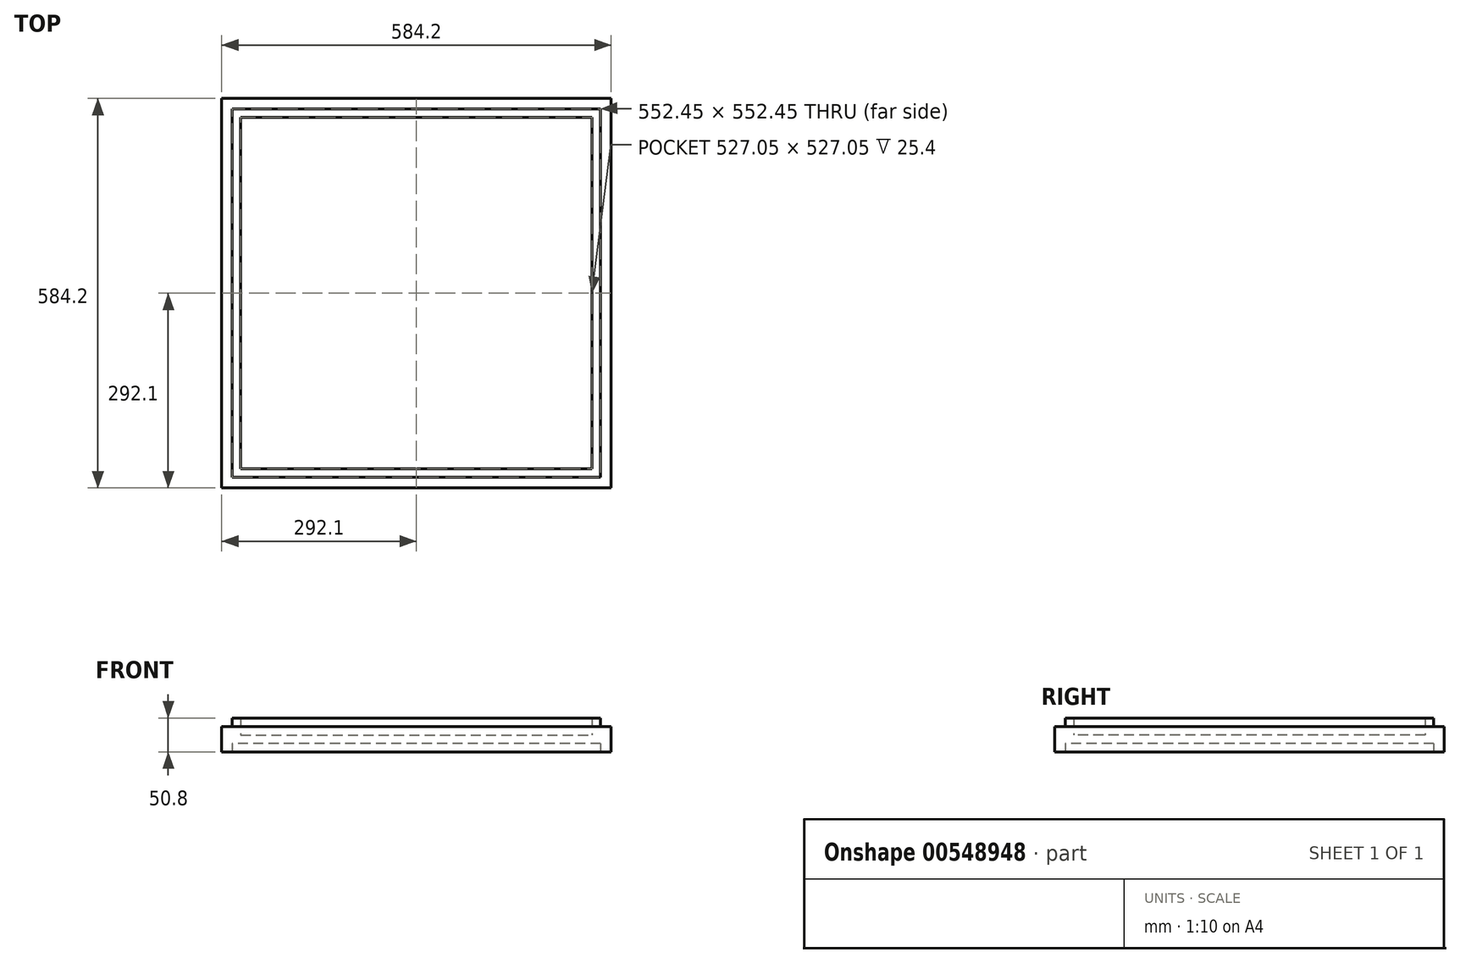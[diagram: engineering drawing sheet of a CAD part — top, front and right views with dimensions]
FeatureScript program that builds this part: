
annotation { "Feature Type Name" : "Feature", "Feature Type Description" : "" }
export const myFeature = defineFeature(function(context is Context, id is Id, definition is map)
    precondition{}
    {
        {
            var Q0;
            Q0=qCreatedBy(makeId("Top.planeOp"),FACE);
            var sketch = newSketch(context, id + "F0", { "sketchPlane" : qUnion([Q0])});
            skLineSegment(sketch, "E0.bottom", {"start": v(-292.1, 292.1) * mm, "end": v(292.1, 292.1) * mm});
            skLineSegment(sketch, "E0.top", {"start": v(-292.1, -292.1) * mm, "end": v(292.1, -292.1) * mm});
            skLineSegment(sketch, "E0.left", {"start": v(-292.1, 292.1) * mm, "end": v(-292.1, -292.1) * mm});
            skLineSegment(sketch, "E0.right", {"start": v(292.1, 292.1) * mm, "end": v(292.1, -292.1) * mm});
            skPoint(sketch, "E0.middle", {"position": v(0, 0) * mm});
            skSolve(sketch);
        }
        {
            var Q0;
            Q0=qSketchRegion(id+"F0",true);
            extrude(context, id + "F1", {"entities" : qUnion([Q0]), "depth" : 12.7 * mm, "offsetDistance" : 25.4 * mm});
        }
        {
            var Q0;
            Q0=makeQuery(id+"F1.opExtrude","CAP_FACE",FACE,{"disambiguationData":[OSD([sQuery(id+"F0.wireOp",EDGE,"E0.bottom"),sQuery(id+"F0.wireOp",EDGE,"E0.top"),sQuery(id+"F0.wireOp",EDGE,"E0.left"),sQuery(id+"F0.wireOp",EDGE,"E0.right")])],"isStart":false});
            var sketch = newSketch(context, id + "F2", { "sketchPlane" : qUnion([Q0])});
            skLineSegment(sketch, "E1.bottom", {"start": v(-292.1, 292.1) * mm, "end": v(292.1, 292.1) * mm});
            skLineSegment(sketch, "E1.top", {"start": v(-292.1, -292.1) * mm, "end": v(292.1, -292.1) * mm});
            skLineSegment(sketch, "E1.left", {"start": v(-292.1, 292.1) * mm, "end": v(-292.1, -292.1) * mm});
            skLineSegment(sketch, "E1.right", {"start": v(292.1, 292.1) * mm, "end": v(292.1, -292.1) * mm});
            skLineSegment(sketch, "E2.bottom", {"start": v(-279.4, 279.4) * mm, "end": v(279.4, 279.4) * mm});
            skLineSegment(sketch, "E2.top", {"start": v(-279.4, -279.4) * mm, "end": v(279.4, -279.4) * mm});
            skLineSegment(sketch, "E2.left", {"start": v(-279.4, 279.4) * mm, "end": v(-279.4, -279.4) * mm});
            skLineSegment(sketch, "E2.right", {"start": v(279.4, 279.4) * mm, "end": v(279.4, -279.4) * mm});
            skSolve(sketch);
        }
        {
            var Q0;
            Q0=qSketchRegion(id+"F2",true);
            extrude(context, id + "F3", {"entities" : qUnion([Q0]), "operationType" : NewBodyOperationType.ADD, "depth" : 152.4 * mm, "offsetDistance" : 25.4 * mm});
        }
        {
            var Q0;
            Q0=makeQuery(id+"F1.opExtrude","CAP_FACE",FACE,{"disambiguationData":[OSD([sQuery(id+"F0.wireOp",EDGE,"E0.bottom"),sQuery(id+"F0.wireOp",EDGE,"E0.top"),sQuery(id+"F0.wireOp",EDGE,"E0.left"),sQuery(id+"F0.wireOp",EDGE,"E0.right")])],"isStart":false});
            var sketch = newSketch(context, id + "F4", { "sketchPlane" : qUnion([Q0])});
            skLineSegment(sketch, "E3.bottom", {"start": v(-508.77, -441.53) * mm, "end": v(508.77, -441.53) * mm});
            skLineSegment(sketch, "E3.top", {"start": v(-508.77, 441.53) * mm, "end": v(508.77, 441.53) * mm});
            skLineSegment(sketch, "E3.left", {"start": v(-508.77, -441.53) * mm, "end": v(-508.77, 441.53) * mm});
            skLineSegment(sketch, "E3.right", {"start": v(508.77, -441.53) * mm, "end": v(508.77, 441.53) * mm});
            skPoint(sketch, "E3.middle", {"position": v(0, 0) * mm});
            skSolve(sketch);
        }
        {
            var Q0;
            Q0=makeQuery(id+"F4.imprint","IMPRINT",FACE,{"disambiguationData":[TD([[makeQuery(id+"F4.imprint","IMPRINT",EDGE,{"derivedFrom":sQuery(id+"F4.wireOp",EDGE,"E3.bottom")}),1.0]])]});
            extrude(context, id + "F5", {"entities" : qUnion([Q0]), "operationType" : NewBodyOperationType.REMOVE, "depth" : 508 * mm, "offsetDistance" : 25.4 * mm});
        }
        {
            var Q0;
            Q0=makeQuery(id+"F5.boolean.opBoolean","MERGE",FACE,{"derivedFrom":[makeQuery(id+"F1.opExtrude","CAP_FACE",FACE,{"disambiguationData":[OSD([sQuery(id+"F0.wireOp",EDGE,"E0.bottom"),sQuery(id+"F0.wireOp",EDGE,"E0.top"),sQuery(id+"F0.wireOp",EDGE,"E0.left"),sQuery(id+"F0.wireOp",EDGE,"E0.right")])],"isStart":false}),makeQuery(id+"F5.opExtrude","CAP_FACE",FACE,{"disambiguationData":[OSD([sQuery(id+"F2.wireOp",EDGE,"E2.bottom"),sQuery(id+"F2.wireOp",EDGE,"E2.top"),sQuery(id+"F2.wireOp",EDGE,"E2.left"),sQuery(id+"F2.wireOp",EDGE,"E2.right"),sQuery(id+"F4.wireOp",EDGE,"E3.bottom"),sQuery(id+"F4.wireOp",EDGE,"E3.top"),sQuery(id+"F4.wireOp",EDGE,"E3.left"),sQuery(id+"F4.wireOp",EDGE,"E3.right")])],"isStart":true})]});
            var sketch = newSketch(context, id + "F6", { "sketchPlane" : qUnion([Q0])});
            skLineSegment(sketch, "E4.bottom", {"start": v(-276.23, -276.23) * mm, "end": v(276.23, -276.23) * mm});
            skLineSegment(sketch, "E4.top", {"start": v(-276.23, 276.23) * mm, "end": v(276.23, 276.23) * mm});
            skLineSegment(sketch, "E4.left", {"start": v(-276.23, -276.23) * mm, "end": v(-276.23, 276.23) * mm});
            skLineSegment(sketch, "E4.right", {"start": v(276.23, -276.23) * mm, "end": v(276.23, 276.23) * mm});
            skPoint(sketch, "E4.middle", {"position": v(0, 0) * mm});
            skLineSegment(sketch, "E5.bottom", {"start": v(-263.53, 263.53) * mm, "end": v(263.53, 263.53) * mm});
            skLineSegment(sketch, "E5.top", {"start": v(-263.53, -263.53) * mm, "end": v(263.53, -263.53) * mm});
            skLineSegment(sketch, "E5.left", {"start": v(-263.53, 263.53) * mm, "end": v(-263.53, -263.53) * mm});
            skLineSegment(sketch, "E5.right", {"start": v(263.53, 263.53) * mm, "end": v(263.53, -263.53) * mm});
            skSolve(sketch);
        }
        {
            var Q0;
            Q0 = qSketchRegion(id + "F6", true);
            extrude(context, id + "F7", {"entities" : qUnion([Q0]), "operationType" : NewBodyOperationType.ADD, "depth" : 25.4 * mm, "offsetDistance" : 25.4 * mm});
        }
        {
            var Q0;
            {var subQ0=sQuery(id+"F0.wireOp",EDGE,"E0.left");var subQ1=sQuery(id+"F0.wireOp",EDGE,"E0.bottom");var subQ2=sQuery(id+"F0.wireOp",EDGE,"E0.right");var subQ3=sQuery(id+"F0.wireOp",EDGE,"E0.top");Q0=makeQuery(id+"F7.boolean.opBoolean","SPLIT",FACE,{"disambiguationData":[TD([makeQuery(id+"F1.opExtrude","SWEPT_FACE",FACE,{"disambiguationData":[OSD([subQ1])]})])],"derivedFrom":makeQuery(id+"F5.boolean.opBoolean","MERGE",FACE,{"derivedFrom":[makeQuery(id+"F1.opExtrude","CAP_FACE",FACE,{"disambiguationData":[OSD([subQ1,subQ3,subQ0,subQ2])],"isStart":false}),makeQuery(id+"F5.opExtrude","CAP_FACE",FACE,{"disambiguationData":[OSD([sQuery(id+"F2.wireOp",EDGE,"E2.bottom"),sQuery(id+"F2.wireOp",EDGE,"E2.top"),sQuery(id+"F2.wireOp",EDGE,"E2.left"),sQuery(id+"F2.wireOp",EDGE,"E2.right"),sQuery(id+"F4.wireOp",EDGE,"E3.bottom"),sQuery(id+"F4.wireOp",EDGE,"E3.top"),sQuery(id+"F4.wireOp",EDGE,"E3.left"),sQuery(id+"F4.wireOp",EDGE,"E3.right")])],"isStart":true})]})});}
            var sketch = newSketch(context, id + "F8", { "sketchPlane" : qUnion([Q0])});
            skLineSegment(sketch, "E6.0", {"start": v(-276.23, -276.23) * mm, "end": v(-276.23, 276.23) * mm});
            skLineSegment(sketch, "E6.1", {"start": v(-276.23, -276.23) * mm, "end": v(276.23, -276.23) * mm});
            skLineSegment(sketch, "E6.2", {"start": v(276.23, -276.23) * mm, "end": v(276.23, 276.23) * mm});
            skLineSegment(sketch, "E6.3", {"start": v(-276.23, 276.23) * mm, "end": v(276.23, 276.23) * mm});
            skLineSegment(sketch, "E6.4", {"start": v(-292.1, 292.1) * mm, "end": v(292.1, 292.1) * mm});
            skLineSegment(sketch, "E6.5", {"start": v(292.1, 292.1) * mm, "end": v(292.1, -292.1) * mm});
            skLineSegment(sketch, "E6.6", {"start": v(-292.1, 292.1) * mm, "end": v(-292.1, -292.1) * mm});
            skLineSegment(sketch, "E6.7", {"start": v(-292.1, -292.1) * mm, "end": v(292.1, -292.1) * mm});
            skSolve(sketch);
        }
        {
            var Q0;
            Q0=makeQuery(id+"F8.imprint","IMPRINT",FACE,{"disambiguationData":[TD([[makeQuery(id+"F8.imprint","IMPRINT",EDGE,{"derivedFrom":sQuery(id+"F8.wireOp",EDGE,"E6.0")}),1.0]])]});
            extrude(context, id + "F9", {"entities" : qUnion([Q0]), "operationType" : NewBodyOperationType.ADD, "depth" : 12.7 * mm, "offsetDistance" : 25.4 * mm, "hasSecondDirection" : true, "secondDirectionOppositeDirection" : true, "secondDirectionDepth" : 25.4 * mm});
        }
    });
